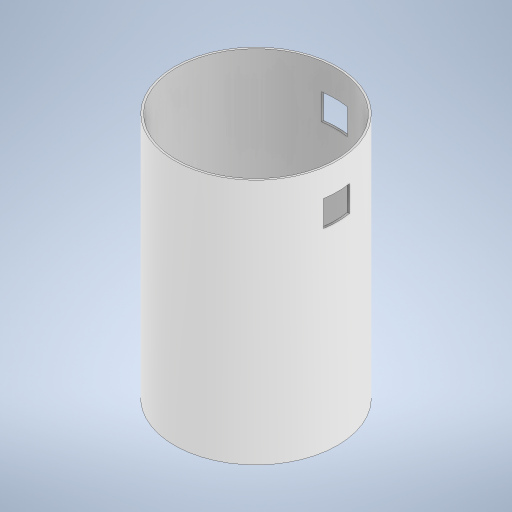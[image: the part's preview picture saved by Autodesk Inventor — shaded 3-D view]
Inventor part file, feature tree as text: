
AUTODESK INVENTOR PART (.ipt)
format: ipt  version: 2024 (Build 280153000, 153)  size: 236,032 bytes
history: native  units: in
note: dims shown in document units (in); Inventor stores cm internally (conversion verified against a paired STEP export)
features: extrude x1, sketch x1
ambient origin geometry x8: Origin, YZ Plane, XZ Plane, XY Plane, X Axis, Y Axis, Z Axis, Center Point
bodies: Solid2 (feature_tree), Solid1 (feature_tree)
feature tree (2):
  extrude  "Extrusion1"  Depth=1.6535in
  sketch  "Sketch1"  dims[d0=1.5748in d1=1.6142in d2=1.6535in d3=0.0in]
